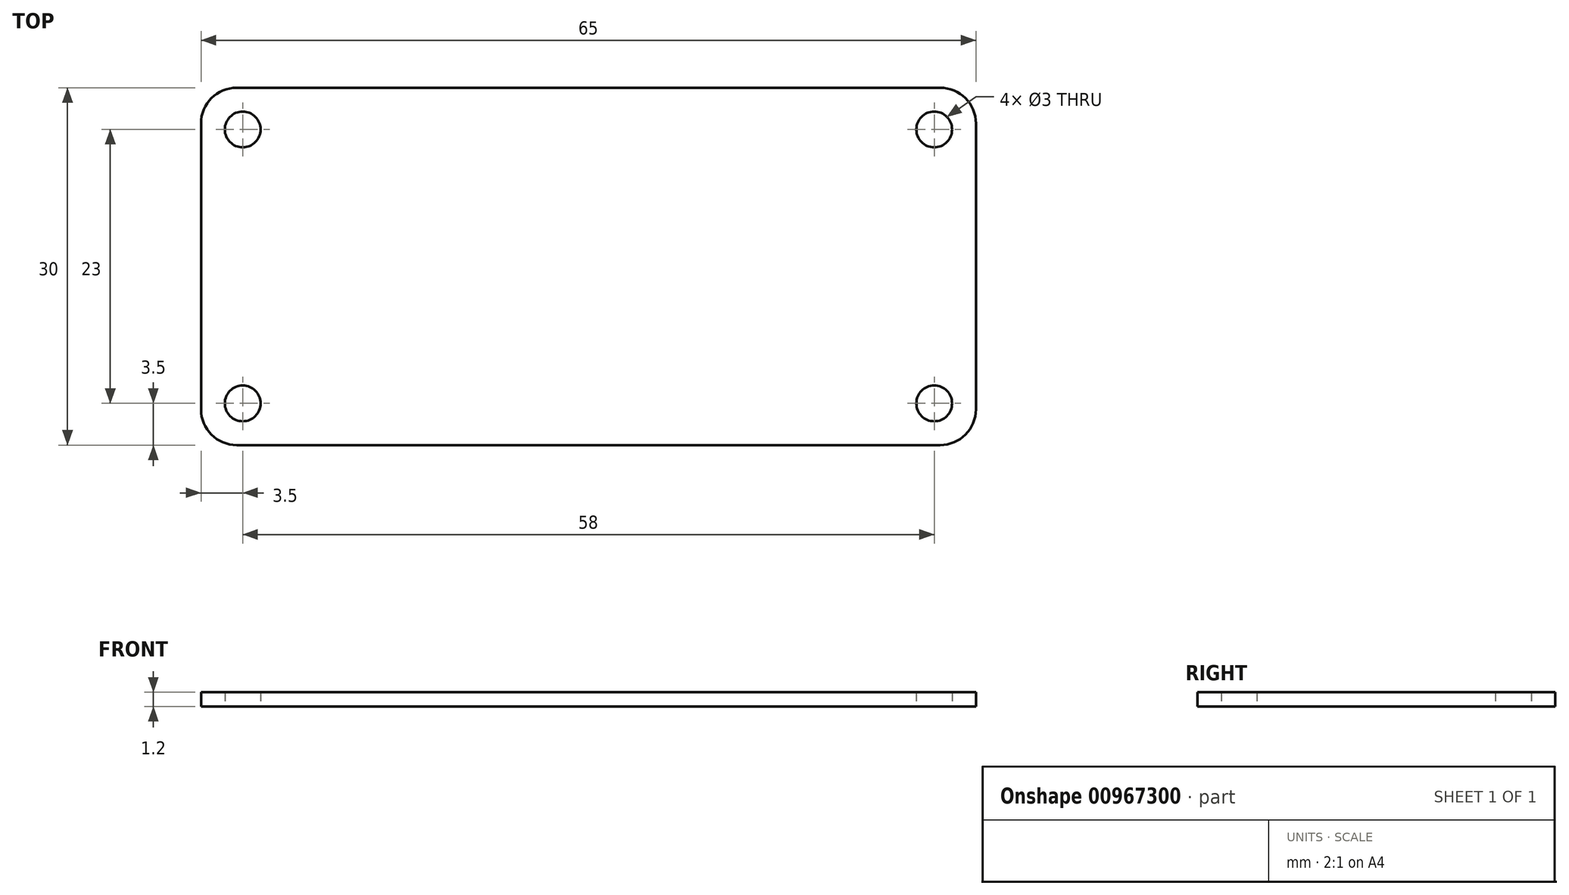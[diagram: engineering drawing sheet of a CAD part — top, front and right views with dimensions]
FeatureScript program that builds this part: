
annotation { "Feature Type Name" : "Feature", "Feature Type Description" : "" }
export const myFeature = defineFeature(function(context is Context, id is Id, definition is map)
    precondition{}
    {
        {
            var Q0;
            Q0=qCreatedBy(makeId("Top.planeOp"),FACE);
            var sketch = newSketch(context, id + "F0", { "sketchPlane" : qUnion([Q0])});
            skLineSegment(sketch, "E0.bottom", {"start": v(29.5, -15) * mm, "end": v(-29.5, -15) * mm});
            skLineSegment(sketch, "E0.top", {"start": v(29.5, 15) * mm, "end": v(-29.5, 15) * mm});
            skLineSegment(sketch, "E0.left", {"start": v(32.5, -12) * mm, "end": v(32.5, 12) * mm});
            skLineSegment(sketch, "E0.right", {"start": v(-32.5, -12) * mm, "end": v(-32.5, 12) * mm});
            skPoint(sketch, "E0.middle", {"position": v(0, 0) * mm});
            skPoint(sketch, "E1.visualSharp", {"position": v(-32.5, 15) * mm});
            skArc(sketch, "E1.filletArc", {"start": v(-29.5, 15) * mm, "mid": v(-31.62, 14.12) * mm, "end": v(-32.5, 12) * mm});
            skPoint(sketch, "E2.visualSharp", {"position": v(32.5, 15) * mm});
            skArc(sketch, "E2.filletArc", {"start": v(32.5, 12) * mm, "mid": v(31.62, 14.12) * mm, "end": v(29.5, 15) * mm});
            skPoint(sketch, "E3.visualSharp", {"position": v(32.5, -15) * mm});
            skArc(sketch, "E3.filletArc", {"start": v(29.5, -15) * mm, "mid": v(31.62, -14.12) * mm, "end": v(32.5, -12) * mm});
            skPoint(sketch, "E4.visualSharp", {"position": v(-32.5, -15) * mm});
            skArc(sketch, "E4.filletArc", {"start": v(-32.5, -12) * mm, "mid": v(-31.62, -14.12) * mm, "end": v(-29.5, -15) * mm});
            skLineSegment(sketch, "E5.bottom", {"start": v(29, -11.5) * mm, "end": v(-29, -11.5) * mm});
            skLineSegment(sketch, "E5.top", {"start": v(29, 11.5) * mm, "end": v(-29, 11.5) * mm});
            skLineSegment(sketch, "E5.left", {"start": v(29, -11.5) * mm, "end": v(29, 11.5) * mm});
            skLineSegment(sketch, "E5.right", {"start": v(-29, -11.5) * mm, "end": v(-29, 11.5) * mm});
            skCircle(sketch, "E6", {"center": v(-29, 11.5) * mm, "radius": 1.5 * mm});
            skCircle(sketch, "E7", {"center": v(-29, -11.5) * mm, "radius": 1.5 * mm});
            skCircle(sketch, "E8", {"center": v(29, -11.5) * mm, "radius": 1.5 * mm});
            skCircle(sketch, "E9", {"center": v(29, 11.5) * mm, "radius": 1.5 * mm});
            skSolve(sketch);
        }
        {
            var Q0;
            Q0=makeQuery(id+"F0.imprint","IMPRINT",FACE,{"disambiguationData":[TD([[makeQuery(id+"F0.imprint","IMPRINT",EDGE,{"derivedFrom":sQuery(id+"F0.wireOp",EDGE,"E0.bottom")}),-1.0]])]});
            var Q1;
            {var subQ5=sQuery(id+"F0.wireOp",EDGE,"E8");var subQ13=sQuery(id+"F0.wireOp",EDGE,"E5.bottom");var subQ14=makeQuery(id+"F0.imprint","INTERSECT",VERTEX,{"derivedFrom":[subQ13,subQ5]});Q1=makeQuery(id+"F0.imprint","IMPRINT",FACE,{"disambiguationData":[TD([[makeQuery(id+"F0.imprint","IMPRINT",EDGE,{"disambiguationData":[TD([[subQ14,-1.0]])],"derivedFrom":subQ13}),-1.0]])]});}
            extrude(context, id + "F1", {"entities" : qUnion([Q0, Q1]), "depth" : 1.2 * mm, "offsetDistance" : 25 * mm});
        }
    });
